# Revit family: Shower-Handshower-KOHLER-Awaken-K-98361
name_source: partatom
category: Plumbing Fixtures
revit_build: Autodesk Revit 2015 (Build: 20140606_1530(x64)
units: mm (PartAtom-declared; Revit-internal decimal feet)

## types (4) — shared parameters
ADA Compliant = No
Assembly Code = D2010700
CW Connection = No
Cold Water Inlet = Cold Water Inlet
Date Modified = 09/18/2018
Default Elevation = 42"
Flow Rate = 2 GPM
HW Connection = Yes
Height = 27 1/4"
Hot Water Inlet = Tempered Water Inlet
Length = 3 7/8"
Manufacturer = KOHLER Co.
MasterFormat 1995 = 15410
MasterFormat 2004 = 22.41.23
Material = Premium Metal Construction
Panel Thickness = 0"
Product Documentation Link = http://www.us.kohler.com
Product Name = Awaken
Product Page URL = http://www.us.kohler.com
URL = https://www.us.kohler.com
Vent Connection = No
Waste Connection = No
Waste Water Outlet = Waste Water Outlet
Width = 5 17/32"

## per-type parameters (varying)
| type | Description | Finish | Model | Type |
| 2.0 GPM, CP-Polished Chrome | G90 2.0 gpm handshower kit | Kohler-Metal-CP-Polished_Chrome | K-98361-CP | 1 |
| 1.75 GPM, CP-Polished Chrome | G90 1.75 gpm handshower kit | Kohler-Metal-CP-Polished_Chrome | K-98361-G-CP | 3 |
| 2.0 GPM, BN-Vibrant Brushed Nickel | G90 2.0 gpm handshower kit | Kohler-Metal-BN-Vibrant_Brushed_Nickel | K-98361-BN | 2 |
| 1.75 GPM, BN-Vibrant Brushed Nickel | G90 1.75 gpm handshower kit | Kohler-Metal-BN-Vibrant_Brushed_Nickel | K-98361-G-BN | 4 |

## geometry (parser evidence)
native form markers: Sweep x3
no freeform markers — native parametric forms only
